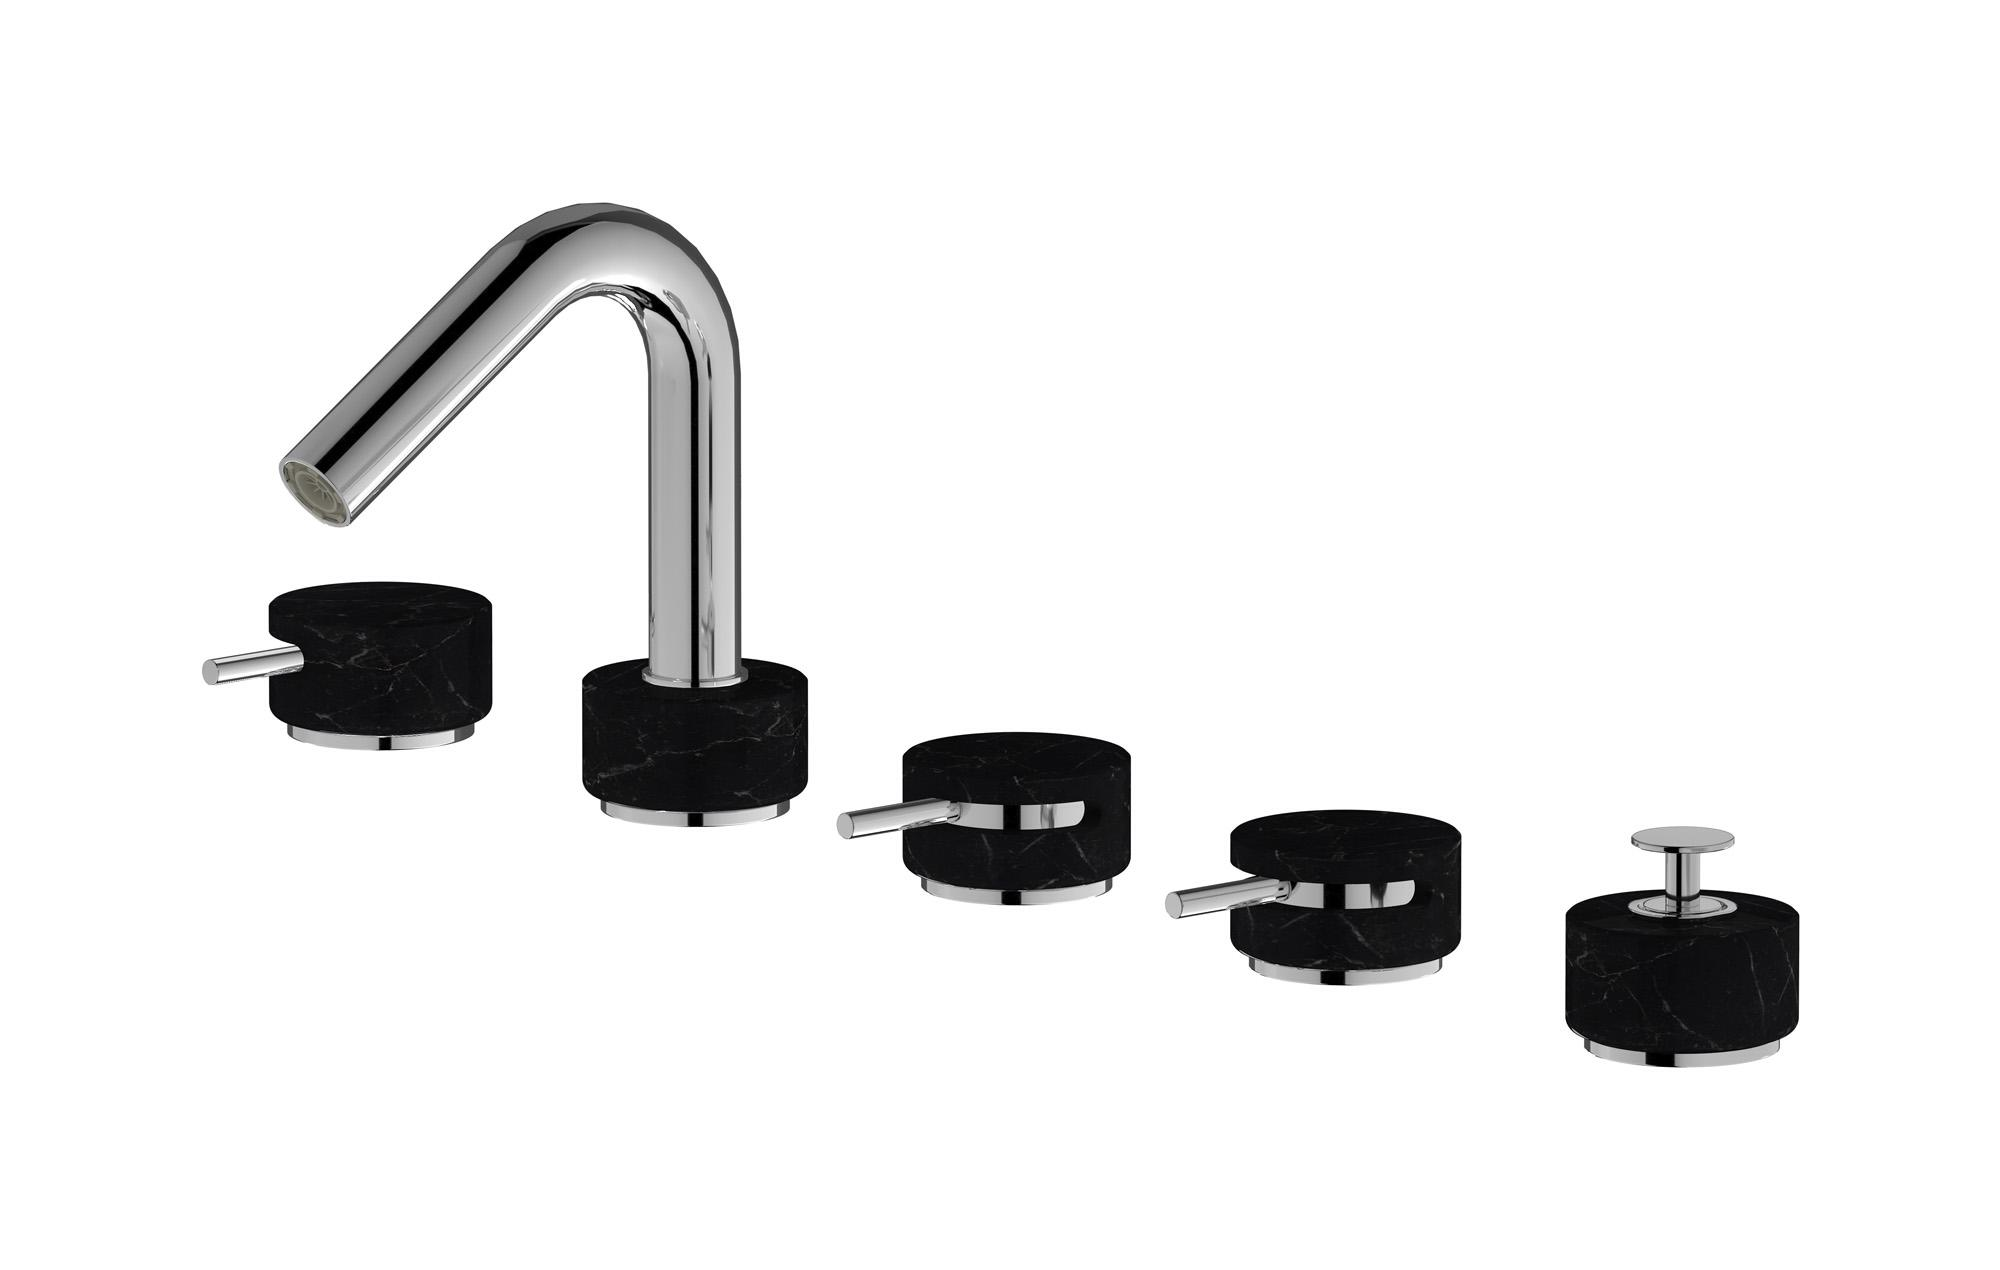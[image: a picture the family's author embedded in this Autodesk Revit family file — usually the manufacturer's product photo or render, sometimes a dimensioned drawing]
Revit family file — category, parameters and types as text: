
# Revit family: MR396_2
name_source: partatom
category: Apparecchi idraulici
units: mm (PartAtom-declared; Revit-internal decimal feet)

## family parameters
Basato su piano di lavoro = No
Condiviso = No
Mantieni orientamento annotazione = No
Numero OmniClass = 23.45.55.17
Punto di calcolo locali = No
Quota connettore circolare = Usa diametro
Sempre verticale = Sì
Taglio con vuoti quando caricato = No
Tipo di parte = Normale
Titolo OmniClass = Mixing Faucets

## types (14) — shared parameters
Cold water inlet = 10 mm  [stored 0.0328084 ft]
Commenti sul tipo = Bath filler
Connessione CW = No
Connessione HW = No
Connessione di scarico = No
Connessione di ventilazione = No
Descrizione = Five holes deck mounted bath filler with shower kit
Hot water inlet = 10 mm  [stored 0.0328084 ft]
Produttore = IB Rubinetterie S.p.A.
URL = https://www.weareib.it
zero-valued in all types: Prospetto di default

## per-type parameters (varying)
| type | Finishes surface | Immagine tipo | Modello |
| Chrome | IB_Chrome | MR396CC_2.jpg | MR396CC_2 |
| Platinum | IB_Platinum | MR396PL_2.jpg | MR396PL_2 |
| Brushed nickel | IB_Brushed nickel | MR396SS_2.jpg | MR396SS_2 |
| Natural brass | IB_Brass | MR396ON_2.jpg | MR396ON_2 |
| Matt white | IB_matt white | MR396BO_2.jpg | MR396BO_2 |
| Matt black | IB_matt black | MR396NP_2.jpg | MR396NP_2 |
| Black chrome | IB_Black chrome | MR396CF_2.jpg | MR396CF_2 |
| Brushed black chrome | IB_Brushed black chrome | MR396CS_2.jpg | MR396CS_2 |
| Pale gold | IB_Pale gold | MR396II_2.jpg | MR396II_2 |
| Brushed pale gold | IB_brushed pale gold | MR396IS_2.jpg | MR396IS_2 |
| Rose gold | IB_Rose gold | MR396RS_2.jpg | MR396RS_2 |
| Brushed rose gold | IB_Brushed rose gold | MR396SR_2.jpg | MR396SR_2 |
| Gold | IB_gold | MR396OO_2.jpg | MR396OO_2 |
| Brushed gold | IB_brushed gold | MR396OS_2.jpg | MR396OS_2 |

note: [stored X ft] marks values corroborated as IEEE doubles in the binary element streams (Revit-internal decimal feet)
